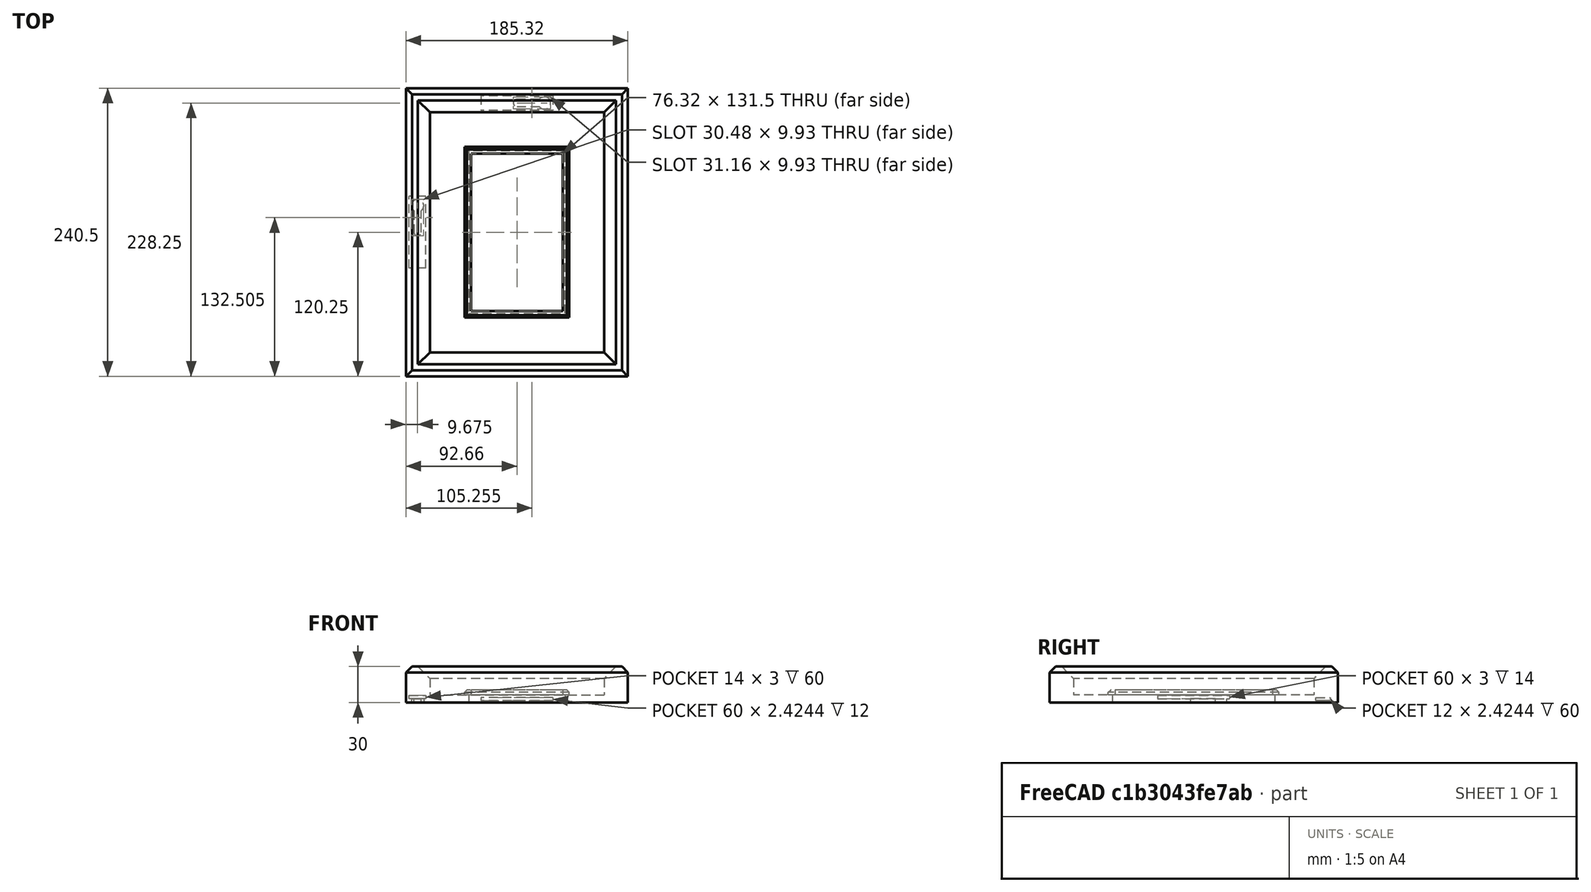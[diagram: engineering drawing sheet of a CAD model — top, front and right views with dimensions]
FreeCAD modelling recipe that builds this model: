
FCSTD DOCUMENT  (FreeCAD 0.21R33771 (Git))
Label: Wall Frame
License: All rights reserved
LicenseURL: http://en.wikipedia.org/wiki/All_rights_reserved
objects: Sketcher::SketchObject×9, PartDesign::Pocket×7, TechDraw::DrawHatch×6, PartDesign::Chamfer×3, TechDraw::DrawViewPart×3, PartDesign::Pad×2, TechDraw::DrawViewDimension×2, Spreadsheet::Sheet×1, PartDesign::Body×1, App::Part×1, TechDraw::DrawSVGTemplate×1, TechDraw::DrawViewAnnotation×1, TechDraw::DrawPage×1
note: 38 computed .brp shape members not serialized (recipe doc carries the construction recipe); baked Part::Feature solids carry a one-line shape summary decoded from their .brp

FEATURE [Sketcher::SketchObject] Sketch  label="Wall Frame Outer Sketch"
  FullyConstrained = true
  MapMode = 5
  Support = -> [XY_Plane001]
  expr: Constraints[10] = Spreadsheet.Frame_Outer_Width
  expr: Constraints[11] = Spreadsheet.Frame_Outer_Length
  sketch-geometry (5):
    g0: LineSegment StartX=-92.66 StartY=120.25 StartZ=0 EndX=-92.66 EndY=-120.25 EndZ=0
    g1: LineSegment StartX=-92.66 StartY=-120.25 StartZ=0 EndX=92.66 EndY=-120.25 EndZ=0
    g2: LineSegment StartX=92.66 StartY=-120.25 StartZ=0 EndX=92.66 EndY=120.25 EndZ=0
    g3: LineSegment StartX=92.66 StartY=120.25 StartZ=0 EndX=-92.66 EndY=120.25 EndZ=0
    g4: GeomPoint X=0 Y=0 Z=0
  constraints (12):
    c: Coincident(g0,g1)
    c: Coincident(g1,g2)
    c: Coincident(g2,g3)
    c: Coincident(g3,g0)
    c: Horizontal(g1)
    c: Horizontal(g3)
    c: Vertical(g0)
    c: Vertical(g2)
    c: Symmetric(g1,g0,g4)
    c: Coincident(g4,g-1)
    c: DistanceX(g3,g3) = 185.32
    c: DistanceY(g2,g2) = 240.5
FEATURE [PartDesign::Pad] Pad  label="Wall Frame Outer Pad"
  Direction = (0,0,1)
  Length = 30
  Length2 = 10
  Profile = -> Sketch
  ReferenceAxis = -> Sketch [N_Axis]
  Type = 0
FEATURE [Spreadsheet::Sheet] Spreadsheet  label="p"
  cells = A1='Frame_Outer_Width; B1(Frame_Outer_Width)=185.32; C1='DO NOT CHANGE; A2='Frame_Outer_Length; B2(Frame_Outer_Length)=240.5; C2='DO NOT CHANGE; A3='Frame_Outer_Thickness; B3(Frame_Outer_Thickness)=30; C3='DO NOT CHANGE; A4='Frame_Outer_Inner_Chamfer; B4(Frame_Outer_Inner_Chamfer)=10; C4='<---   YOU MAY CHANGE; A5='Frame_Outer_Outer_Chamfer; B5(Frame_Outer_Outer_Chamfer)=5; C5='<---   YOU MAY CHANGE; A7='Frame_First_Inner_Pocket_Width; B7(card_holder_width)=145.32; C7='DO NOT CHANGE; A8='Frame_First_Inner_Pocket_Length; B8(card_holder_length)=200.5; C8='DO NOT CHANGE; A9='card_holder_thickness; B9(card_holder_thickness)=6.4; C9='SHOULD MATCH; G9=6.4; H9='"+1"; A10='Frame_First_Inner_Pocket_Depth; B10(Frame_First_Inner_Pocket)==B3 - B14; C10='DO NOT CHANGE; G11='PSA Normal Card; H11='PSA Topps Giants Card; A12='PSA_Frame_Width; B12(PSA_Frame_Width)=80.32; C12='<---   YOU MAY CHANGE; G12=80.32; H12=108; A13='PSA_Frame_Length; B13(PSA_Frame_Length)=135.5; C13='<---   YOU MAY CHANGE; G13=135.5; H13=184.3; A14='PSA_Frame_Thickness; B14(PSA_Frame_Thickness)=6.4; C14='SHOULD MATCH; G14=6.4; H14='"+1"; A16='Frame_PSA_Border_Height; B16(Frame_PSA_Border_Height)=5; C16='<---   YOU MAY CHANGE; G16=4; H16='"+1"; A17='Frame_PSA_Border_Chamfer; B17(Frame_PSA_Border_Chamfer)=2; C17='<---   YOU MAY CHANGE; D17='Must be at least 1mm less "Frame_PSA_Border_Height", may not be same; G17=3; G19='GEM Normal; G20=83.82; G21=131.76
FEATURE [Sketcher::SketchObject] Sketch003  label="Wall Frame First Inner Sketch"
  AttachmentOffset = pos=(0,0,30) rot=(0,0,1;0rad)
  FullyConstrained = true
  MapMode = 5
  Placement = pos=(0,0,30) rot=(0,0,1;0rad)
  Support = -> [XY_Plane001]
  expr: Constraints[10] = <<p>>.card_holder_width
  expr: Constraints[11] = <<p>>.card_holder_length
  sketch-geometry (5):
    g0: LineSegment StartX=-72.66 StartY=100.25 StartZ=0 EndX=-72.66 EndY=-100.25 EndZ=0
    g1: LineSegment StartX=-72.66 StartY=-100.25 StartZ=0 EndX=72.66 EndY=-100.25 EndZ=0
    g2: LineSegment StartX=72.66 StartY=-100.25 StartZ=0 EndX=72.66 EndY=100.25 EndZ=0
    g3: LineSegment StartX=72.66 StartY=100.25 StartZ=0 EndX=-72.66 EndY=100.25 EndZ=0
    g4: GeomPoint X=0 Y=0 Z=0
  constraints (12):
    c: Coincident(g0,g1)
    c: Coincident(g1,g2)
    c: Coincident(g2,g3)
    c: Coincident(g3,g0)
    c: Horizontal(g1)
    c: Horizontal(g3)
    c: Vertical(g0)
    c: Vertical(g2)
    c: Symmetric(g1,g0,g4)
    c: Coincident(g4,g-1)
    c: DistanceX(g3,g3) = 145.32
    c: DistanceY(g2,g2) = 200.5
FEATURE [PartDesign::Pocket] Pocket  label="Wall Frame First Inner Pocket"
  BaseFeature = -> Pad
  Direction = (0,0,-1)
  Length = 23.6
  Length2 = 5
  Profile = -> Sketch003
  ReferenceAxis = -> Sketch003 [N_Axis]
  Type = 0
  expr: Length = <<p>>.Frame_First_Inner_Pocket
FEATURE [Sketcher::SketchObject] Sketch004  label="Wall Frame PSA Sketch"
  AttachmentOffset = pos=(0,0,6.4) rot=(0,0,1;0rad)
  FullyConstrained = true
  MapMode = 5
  Placement = pos=(0,0,6.4) rot=(0,0,1;0rad)
  Support = -> [XY_Plane001]
  expr: .AttachmentOffset.Base.z = <<p>>.card_holder_thickness
  expr: Constraints[10] = Spreadsheet.PSA_Frame_Width
  expr: Constraints[11] = Spreadsheet.PSA_Frame_Length
  sketch-geometry (5):
    g0: LineSegment StartX=-40.16 StartY=67.75 StartZ=0 EndX=-40.16 EndY=-67.75 EndZ=0
    g1: LineSegment StartX=-40.16 StartY=-67.75 StartZ=0 EndX=40.16 EndY=-67.75 EndZ=0
    g2: LineSegment StartX=40.16 StartY=-67.75 StartZ=0 EndX=40.16 EndY=67.75 EndZ=0
    g3: LineSegment StartX=40.16 StartY=67.75 StartZ=0 EndX=-40.16 EndY=67.75 EndZ=0
    g4: GeomPoint X=0 Y=0 Z=0
  constraints (12):
    c: Coincident(g0,g1)
    c: Coincident(g1,g2)
    c: Coincident(g2,g3)
    c: Coincident(g3,g0)
    c: Horizontal(g1)
    c: Horizontal(g3)
    c: Vertical(g0)
    c: Vertical(g2)
    c: Symmetric(g1,g0,g4)
    c: Coincident(g4,g-1)
    c: DistanceX(g3,g3) = 80.32
    c: DistanceY(g2,g2) = 135.5
FEATURE [PartDesign::Pocket] Pocket001  label="Wall Frame PSA Pocket"
  BaseFeature = -> Pocket
  Direction = (0,0,-1)
  Length = 6.4
  Length2 = 5
  Profile = -> Sketch004
  ReferenceAxis = -> Sketch004 [N_Axis]
  Type = 0
  expr: Length = <<p>>.PSA_Frame_Thickness
FEATURE [Sketcher::SketchObject] Sketch005  label="Wall Frame Landscape Screw Sketch"
  FullyConstrained = true
  MapMode = 5
  Support = -> [XY_Plane001]
  sketch-geometry (4):
    g0: ArcOfCircle CenterX=-82.985 CenterY=0 CenterZ=0 NormalX=0 NormalY=0 NormalZ=1 AngleXU=0 Radius=2.985 StartAngle=3.14159 EndAngle=6.28319
    g1: LineSegment StartX=-80 StartY=-7e-16 StartZ=0 EndX=-80 EndY=18.026 EndZ=0
    g2: LineSegment StartX=-85.97 StartY=18.026 StartZ=0 EndX=-85.97 EndY=0 EndZ=0
    g3: ArcOfCircle CenterX=-82.985 CenterY=22.29 CenterZ=0 NormalX=0 NormalY=0 NormalZ=1 AngleXU=0 Radius=5.205 StartAngle=5.32315 EndAngle=10.3848
  constraints (12):
    c: Tangent(g0,g1) = -1.5708
    c: Tangent(g2,g0) = -1.5708
    c: PointOnObject(g0,g-1)
    c: Vertical(g1)
    c: Diameter(g3) = 10.41
    c: Coincident(g3,g2)
    c: Coincident(g3,g1)
    c: Horizontal(g2,g1)
    c: Vertical(g2)
    c: DistanceX(g0,g-1) = 80
    c: DistanceY(g0,g3) = 22.29
    c: Diameter(g0) = 5.97
FEATURE [PartDesign::Pocket] Pocket002  label="Wall Frame Landscape Screw Pocket"
  BaseFeature = -> Pocket001
  Direction = (0,0,-1)
  Length = 3
  Length2 = 5
  Profile = -> Sketch005
  ReferenceAxis = -> Sketch005 [N_Axis]
  Reversed = true
  Type = 0
FEATURE [Sketcher::SketchObject] Sketch006  label="Wall Frame Landscape Screw Head Relief Sketch"
  FullyConstrained = true
  MapMode = 5
  Placement = pos=(0,0,0) rot=(1,0,0;1.5708rad)
  Support = -> [XZ_Plane001]
  sketch-geometry (4):
    g0: LineSegment StartX=-90 StartY=5.98 StartZ=0 EndX=-76 EndY=5.98 EndZ=0
    g1: LineSegment StartX=-76 StartY=5.98 StartZ=0 EndX=-76 EndY=2.98 EndZ=0
    g2: LineSegment StartX=-76 StartY=2.98 StartZ=0 EndX=-90 EndY=2.98 EndZ=0
    g3: LineSegment StartX=-90 StartY=2.98 StartZ=0 EndX=-90 EndY=5.98 EndZ=0
  constraints (12):
    c: Coincident(g0,g1)
    c: Coincident(g1,g2)
    c: Coincident(g2,g3)
    c: Coincident(g3,g0)
    c: Horizontal(g0)
    c: Horizontal(g2)
    c: Vertical(g1)
    c: Vertical(g3)
    c: DistanceX(g1,g-1) = 76
    c: DistanceX(g2,g-1) = 90
    c: DistanceY(g3,g3) = 3
    c: DistanceY(g-1,g1) = 2.98
FEATURE [PartDesign::Pocket] Pocket003  label="Wall Frame Landscape Screw Head Relief Pocket"
  BaseFeature = -> Pocket002
  Direction = (0,1,2e-16)
  Length = 60
  Length2 = 5
  Midplane = true
  Profile = -> Sketch006
  ReferenceAxis = -> Sketch006 [N_Axis]
  Type = 0
FEATURE [Sketcher::SketchObject] Sketch007  label="Wall Frame Portrait Screw Sketch"
  FullyConstrained = true
  MapMode = 5
  Support = -> [XY_Plane001]
  sketch-geometry (4):
    g0: ArcOfCircle CenterX=0 CenterY=108 CenterZ=0 NormalX=0 NormalY=0 NormalZ=1 AngleXU=0 Radius=2.985 StartAngle=1.5708 EndAngle=4.71239
    g1: LineSegment StartX=-5e-16 StartY=105.015 StartZ=0 EndX=18.706 EndY=105.015 EndZ=0
    g2: LineSegment StartX=18.706 StartY=110.985 StartZ=0 EndX=0 EndY=110.985 EndZ=0
    g3: ArcOfCircle CenterX=22.97 CenterY=108 CenterZ=0 NormalX=0 NormalY=0 NormalZ=1 AngleXU=0 Radius=5.205 StartAngle=3.75235 EndAngle=8.81402
  constraints (12):
    c: Tangent(g0,g1) = -1.5708
    c: Tangent(g2,g0) = -1.5708
    c: PointOnObject(g0,g-2)
    c: Horizontal(g2)
    c: Diameter(g0) = 5.97
    c: DistanceY(g-1,g0) = 108
    c: Diameter(g3) = 10.41
    c: Coincident(g3,g2)
    c: Coincident(g3,g1)
    c: Horizontal(g1)
    c: Vertical(g1,g2)
    c: DistanceX(g0,g3) = 22.97
FEATURE [PartDesign::Pocket] Pocket004  label="Wall Frame Portrait Screw Pocket"
  BaseFeature = -> Pocket003
  Direction = (0,0,-1)
  Length = 3
  Length2 = 5
  Midplane = true
  Profile = -> Sketch007
  ReferenceAxis = -> Sketch007 [N_Axis]
  Type = 0
FEATURE [Sketcher::SketchObject] Sketch008  label="Wall Frame Portrait Screw Head Relief Sketch"
  FullyConstrained = true
  MapMode = 5
  Placement = pos=(0,0,0) rot=(0.57735,0.57735,0.57735;2.0944rad)
  Support = -> [YZ_Plane001]
  sketch-geometry (4):
    g0: LineSegment StartX=102 StartY=3.9227 StartZ=0 EndX=114 EndY=3.9227 EndZ=0
    g1: LineSegment StartX=114 StartY=3.9227 StartZ=0 EndX=114 EndY=1.4983 EndZ=0
    g2: LineSegment StartX=114 StartY=1.4983 StartZ=0 EndX=102 EndY=1.4983 EndZ=0
    g3: LineSegment StartX=102 StartY=1.4983 StartZ=0 EndX=102 EndY=3.9227 EndZ=0
  constraints (12):
    c: Coincident(g0,g1)
    c: Coincident(g1,g2)
    c: Coincident(g2,g3)
    c: Coincident(g3,g0)
    c: Horizontal(g0)
    c: Horizontal(g2)
    c: Vertical(g1)
    c: Vertical(g3)
    c: DistanceX(g-1,g2) = 102
    c: DistanceX(g-1,g1) = 114
    c: DistanceY(g-1,g0) = 3.9227
    c: DistanceY(g-1,g2) = 1.4983
FEATURE [PartDesign::Pocket] Pocket005  label="Wall Frame Portrait Screw Head Relief Pocket"
  BaseFeature = -> Pocket004
  Direction = (-1,2e-16,-3e-16)
  Length = 60
  Length2 = 5
  Midplane = true
  Profile = -> Sketch008
  ReferenceAxis = -> Sketch008 [N_Axis]
  Type = 0
FEATURE [Sketcher::SketchObject] Sketch009  label="Wall Frame PSA Border Outer Sketch"
  AttachmentOffset = pos=(0,0,6.4) rot=(0,0,1;0rad)
  FullyConstrained = true
  MapMode = 5
  Placement = pos=(0,0,6.4) rot=(0,0,1;0rad)
  Support = -> [XY_Plane001]
  expr: .AttachmentOffset.Base.z = <<p>>.card_holder_thickness
  expr: Constraints[10] = Spreadsheet.PSA_Frame_Width + 7
  expr: Constraints[11] = Spreadsheet.PSA_Frame_Length + 7
  sketch-geometry (5):
    g0: LineSegment StartX=-43.66 StartY=71.25 StartZ=0 EndX=-43.66 EndY=-71.25 EndZ=0
    g1: LineSegment StartX=-43.66 StartY=-71.25 StartZ=0 EndX=43.66 EndY=-71.25 EndZ=0
    g2: LineSegment StartX=43.66 StartY=-71.25 StartZ=0 EndX=43.66 EndY=71.25 EndZ=0
    g3: LineSegment StartX=43.66 StartY=71.25 StartZ=0 EndX=-43.66 EndY=71.25 EndZ=0
    g4: GeomPoint X=0 Y=0 Z=0
  constraints (12):
    c: Coincident(g0,g1)
    c: Coincident(g1,g2)
    c: Coincident(g2,g3)
    c: Coincident(g3,g0)
    c: Horizontal(g1)
    c: Horizontal(g3)
    c: Vertical(g0)
    c: Vertical(g2)
    c: Symmetric(g1,g0,g4)
    c: Coincident(g4,g-1)
    c: DistanceX(g3,g3) = 87.32
    c: DistanceY(g2,g2) = 142.5
FEATURE [PartDesign::Pad] Pad001  label="Wall Frame PSA Border Outer Pad"
  BaseFeature = -> Pocket005
  Direction = (0,0,1)
  Length = 4
  Length2 = 10
  Profile = -> Sketch009
  ReferenceAxis = -> Sketch009 [N_Axis]
  Type = 0
FEATURE [Sketcher::SketchObject] Sketch010  label="Wall Frame PSA Border Inner Sketch"
  FullyConstrained = true
  MapMode = 5
  Support = -> [XY_Plane001]
  expr: Constraints[10] = Spreadsheet.PSA_Frame_Width - 4
  expr: Constraints[11] = Spreadsheet.PSA_Frame_Length - 4
  sketch-geometry (5):
    g0: LineSegment StartX=-38.16 StartY=65.75 StartZ=0 EndX=-38.16 EndY=-65.75 EndZ=0
    g1: LineSegment StartX=-38.16 StartY=-65.75 StartZ=0 EndX=38.16 EndY=-65.75 EndZ=0
    g2: LineSegment StartX=38.16 StartY=-65.75 StartZ=0 EndX=38.16 EndY=65.75 EndZ=0
    g3: LineSegment StartX=38.16 StartY=65.75 StartZ=0 EndX=-38.16 EndY=65.75 EndZ=0
    g4: GeomPoint X=0 Y=0 Z=0
  constraints (12):
    c: Coincident(g0,g1)
    c: Coincident(g1,g2)
    c: Coincident(g2,g3)
    c: Coincident(g3,g0)
    c: Horizontal(g1)
    c: Horizontal(g3)
    c: Vertical(g0)
    c: Vertical(g2)
    c: Symmetric(g1,g0,g4)
    c: Coincident(g4,g-1)
    c: DistanceX(g3,g3) = 76.32
    c: DistanceY(g2,g2) = 131.5
FEATURE [PartDesign::Pocket] Pocket006  label="Wall Frame PSA Border Inner Pocket"
  BaseFeature = -> Pad001
  Direction = (0,0,-1)
  Length = 5
  Length2 = 5
  Midplane = true
  Profile = -> Sketch010
  ReferenceAxis = -> Sketch010 [N_Axis]
  Type = 1
FEATURE [PartDesign::Chamfer] Chamfer  label="Wall Frame Outer Inner Chamfer"
  Angle = 45
  Base = -> Pocket006 [Edge25,Edge28,Edge27,Edge26]
  BaseFeature = -> Pocket006
  ChamferType = 0
  FlipDirection = false
  Size = 10
  Size2 = 1
  SupportTransform = false
  UseAllEdges = false
FEATURE [PartDesign::Chamfer] Chamfer001  label="Wall Frame Outer Outer Chamfer"
  Angle = 45
  Base = -> Chamfer [Edge6,Edge5,Edge7,Edge8]
  BaseFeature = -> Chamfer
  ChamferType = 0
  FlipDirection = false
  Size = 5
  Size2 = 1
  SupportTransform = false
  UseAllEdges = false
FEATURE [PartDesign::Chamfer] Chamfer002  label="Wall Frame PSA Border Chamfer"
  Angle = 45
  Base = -> Chamfer001 [Edge83,Edge85,Edge87,Edge88]
  BaseFeature = -> Chamfer001
  ChamferType = 0
  FlipDirection = false
  Size = 2
  Size2 = 1
  SupportTransform = false
  UseAllEdges = false
  expr: Size = <<p>>.Frame_PSA_Border_Chamfer
FEATURE [PartDesign::Body] Body  label="Wall Frame Body"
  Group = -> [Sketch,Pad,Sketch003,Pocket,Sketch004,Pocket001,Sketch005,Pocket002,Sketch006,Pocket003,Sketch007,Pocket004,Sketch008,Pocket005,Sketch009,Pad001,Sketch010,Pocket006,Chamfer,Chamfer001,Chamfer002]
  Origin = -> Origin001
  Tip = -> Chamfer002
FEATURE [App::Part] Part  label="Wall Frame Part"
  Group = -> [Body]
  Origin = -> Origin
FEATURE [TechDraw::DrawSVGTemplate] Template
  Height = 215.9
  Orientation = 1
  Template = C:/Program Files/FreeCAD 0.21/data/Mod/TechDraw/Templates/USLetter_Landscape_blank.svg
  Width = 279.4
FEATURE [TechDraw::DrawViewPart] View  label="Iso View"
  Caption = Iso View
  CoarseView = false
  Direction = (0.57735,-0.57735,0.57735)
  Focus = 100
  HardHidden = false
  IsoCount = 0
  IsoHidden = false
  IsoVisible = false
  LockPosition = false
  Perspective = false
  Rotation = 0
  Scale = 0.55
  ScaleType = 2
  ScrubCount = 0
  SeamHidden = false
  SeamVisible = false
  SmoothHidden = false
  SmoothVisible = true
  Source = -> [Chamfer002]
  X = 187.208
  XDirection = (0.707107,0.707107,0)
  Y = 150.958
FEATURE [TechDraw::DrawViewPart] View001  label="Front View"
  Caption = Front View
  CoarseView = false
  Direction = (0,0,1)
  Focus = 100
  HardHidden = false
  IsoCount = 0
  IsoHidden = false
  IsoVisible = false
  LockPosition = false
  Perspective = false
  Rotation = 0
  Scale = 0.4
  ScaleType = 2
  ScrubCount = 0
  SeamHidden = false
  SeamVisible = false
  SmoothHidden = false
  SmoothVisible = true
  Source = -> [Chamfer002]
  X = 55.4394
  XDirection = (1,0,0)
  Y = 150.876
FEATURE [TechDraw::DrawHatch] Hatch  label="HatchF3"
  HatchPattern = C:/Program Files/FreeCAD 0.21/data/Mod/TechDraw/Patterns/cross.svg
  Source = -> View001 [Face3]
FEATURE [TechDraw::DrawViewPart] View002  label="Back View"
  Caption = Back View
  CoarseView = false
  Direction = (0,0,-1)
  Focus = 100
  HardHidden = false
  IsoCount = 0
  IsoHidden = false
  IsoVisible = false
  LockPosition = false
  Perspective = false
  Rotation = 0
  Scale = 0.4
  ScaleType = 2
  ScrubCount = 0
  SeamHidden = false
  SeamVisible = false
  SmoothHidden = false
  SmoothVisible = true
  Source = -> [Chamfer002]
  X = 61.3831
  XDirection = (0,-1,0)
  Y = 49.0704
FEATURE [TechDraw::DrawHatch] Hatch001  label="Hatch001F9"
  HatchPattern = C:/Program Files/FreeCAD 0.21/data/Mod/TechDraw/Patterns/cuprous.svg
  Source = -> View001 [Face9,Face8,Face10,Face7]
FEATURE [TechDraw::DrawHatch] Hatch002  label="Hatch002F10"
  HatchPattern = C:/Program Files/FreeCAD 0.21/data/Mod/TechDraw/Patterns/cuprous.svg
  Source = -> View [Face10,Face11]
FEATURE [TechDraw::DrawHatch] Hatch003  label="Hatch003F11"
  HatchPattern = C:/Program Files/FreeCAD 0.21/data/Mod/TechDraw/Patterns/line.svg
  Source = -> View001 [Face11,Face13,Face12,Face14]
FEATURE [TechDraw::DrawHatch] Hatch004  label="Hatch004F12"
  HatchPattern = C:/Program Files/FreeCAD 0.21/data/Mod/TechDraw/Patterns/line.svg
  Source = -> View [Face12,Face14]
FEATURE [TechDraw::DrawViewAnnotation] Annotation
  Font = osifont
  LineSpace = 100
  LockPosition = false
  MaxWidth = -1
  Rotation = 0
  ScaleType = 0
  Text = Blue Hatching - Frame Outer Chamfer | Red Hatching - Frame Inner Chamfer | Green Hatching - Card Slab Window Field
  TextSize = 5
  TextStyle = 0
  X = 202.329
  Y = 54.4494
FEATURE [TechDraw::DrawHatch] Hatch005  label="Hatch005F3"
  HatchPattern = C:/Program Files/FreeCAD 0.21/data/Mod/TechDraw/Patterns/cross.svg
  Source = -> View [Face3]
FEATURE [TechDraw::DrawViewDimension] Dimension
  AngleOverride = false
  Arbitrary = false
  ArbitraryTolerances = false
  EqualTolerance = true
  ExtensionAngle = 0
  FormatSpec = %.2w
  FormatSpecOverTolerance = %+.2w
  FormatSpecUnderTolerance = %+.2w
  Inverted = false
  LineAngle = 0
  LockPosition = false
  MeasureType = 1
  OverTolerance = 0
  References2D = -> [View001]
  Rotation = 0
  ScaleType = 0
  TheoreticalExact = false
  Type = 1
  UnderTolerance = 0
  X = 13.4183
  Y = 58.8973
FEATURE [TechDraw::DrawViewDimension] Dimension001
  AngleOverride = false
  Arbitrary = false
  ArbitraryTolerances = false
  EqualTolerance = true
  ExtensionAngle = 0
  FormatSpec = %.2w
  FormatSpecOverTolerance = %+.2w
  FormatSpecUnderTolerance = %+.2w
  Inverted = false
  LineAngle = 0
  LockPosition = false
  MeasureType = 1
  OverTolerance = 0
  References2D = -> [View001]
  Rotation = 0
  ScaleType = 0
  TheoreticalExact = false
  Type = 2
  UnderTolerance = 0
  X = -46.561
  Y = 29.3538
FEATURE [TechDraw::DrawPage] Page
  KeepUpdated = true
  NextBalloonIndex = 1
  ProjectionType = 0
  Template = -> Template
  Views = -> [View,View001,View002,Annotation,Dimension,Dimension001]
